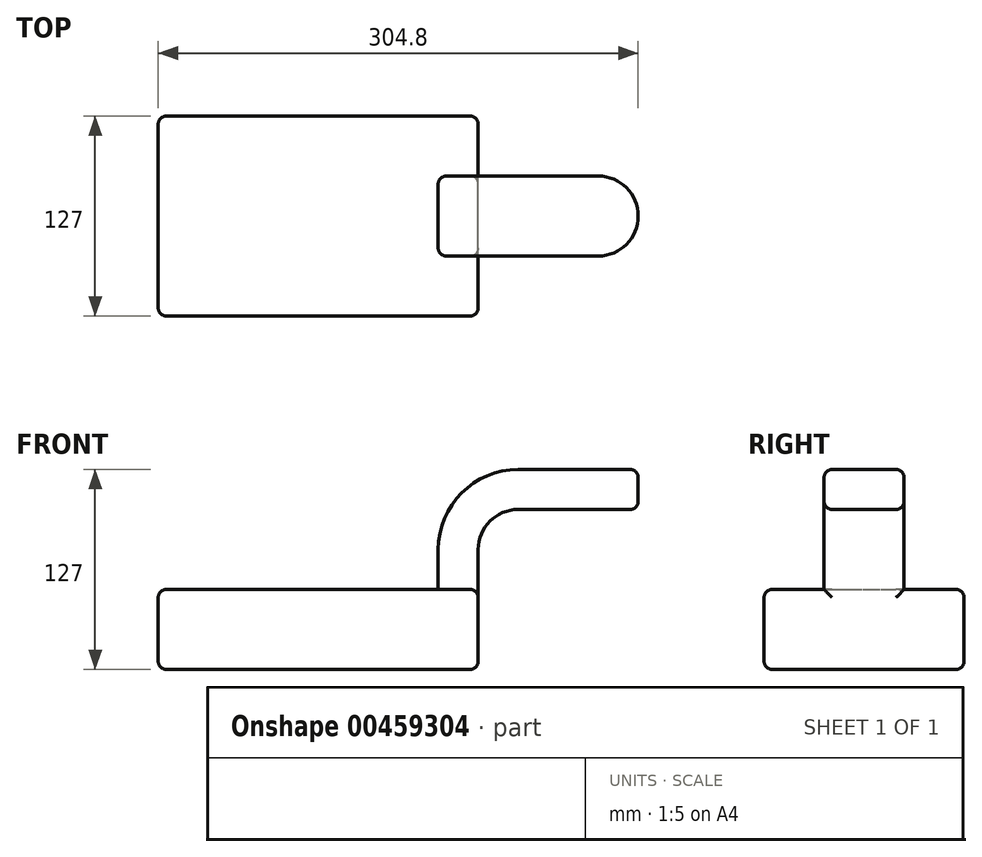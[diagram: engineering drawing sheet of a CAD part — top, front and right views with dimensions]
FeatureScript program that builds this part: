
annotation { "Feature Type Name" : "Feature", "Feature Type Description" : "" }
export const myFeature = defineFeature(function(context is Context, id is Id, definition is map)
    precondition{}
    {
        {
            var Q0;
            Q0=qCreatedBy(makeId("Front.planeOp"),FACE);
            var sketch = newSketch(context, id + "F0", { "sketchPlane" : qUnion([Q0])});
            skLineSegment(sketch, "E0.bottom", {"start": v(-101.6, -25.4) * mm, "end": v(101.6, -25.4) * mm});
            skLineSegment(sketch, "E0.top", {"start": v(-101.6, 25.4) * mm, "end": v(101.6, 25.4) * mm});
            skLineSegment(sketch, "E0.left", {"start": v(-101.6, -25.4) * mm, "end": v(-101.6, 25.4) * mm});
            skLineSegment(sketch, "E0.right", {"start": v(101.6, -25.4) * mm, "end": v(101.6, 25.4) * mm});
            skPoint(sketch, "E0.middle", {"position": v(0, 0) * mm});
            skLineSegment(sketch, "E1.bottom", {"start": v(152.4, 76.2) * mm, "end": v(203.2, 76.2) * mm});
            skLineSegment(sketch, "E1.top", {"start": v(152.4, 127) * mm, "end": v(203.2, 127) * mm});
            skLineSegment(sketch, "E1.left", {"start": v(152.4, 76.2) * mm, "end": v(152.4, 127) * mm});
            skLineSegment(sketch, "E1.right", {"start": v(203.2, 76.2) * mm, "end": v(203.2, 127) * mm});
            skPoint(sketch, "E1.middle", {"position": v(177.8, 101.6) * mm});
            skLineSegment(sketch, "E2", {"start": v(101.6, 25.4) * mm, "end": v(101.6, 50.8) * mm});
            skArc(sketch, "E3", {"start": v(101.6, 50.8) * mm, "mid": v(109.04, 68.76) * mm, "end": v(127, 76.2) * mm});
            skLineSegment(sketch, "E4", {"start": v(127, 76.2) * mm, "end": v(177.8, 76.2) * mm});
            skPoint(sketch, "E4.endSnap0", {"position": v(177.8, 76.2) * mm});
            skLineSegment(sketch, "E5.0", {"start": v(127, 101.6) * mm, "end": v(177.8, 101.6) * mm});
            skArc(sketch, "E5.1", {"start": v(76.2, 50.8) * mm, "mid": v(91.08, 86.72) * mm, "end": v(127, 101.6) * mm});
            skLineSegment(sketch, "E5.2", {"start": v(76.2, 25.4) * mm, "end": v(76.2, 50.8) * mm});
            skLineSegment(sketch, "E6", {"start": v(177.8, 101.6) * mm, "end": v(177.8, 76.2) * mm});
            skFitSpline(sketch, "E7", {"points": [v(127, 101.6) * mm, v(-101.6, 25.4) * mm], "startDerivative": vector(-2.3, 149.1) * mm, "endDerivative": vector(-228.6, -76.2) * mm});
            skLineSegment(sketch, "E8", {"start": v(177.8, 101.6) * mm, "end": v(177.8, 127) * mm});
            skSolve(sketch);
        }
        {
            var Q0;
            Q0=makeQuery(id+"F0.imprint","IMPRINT",FACE,{"disambiguationData":[TD([[makeQuery(id+"F0.imprint","IMPRINT",EDGE,{"derivedFrom":sQuery(id+"F0.wireOp",EDGE,"E0.bottom")}),1.0]])]});
            extrude(context, id + "F1", {"entities" : qUnion([Q0]), "endBound" : BoundingType.SYMMETRIC, "depth" : 127 * mm});
        }
        {
            var Q0;
            {var subQ1=sQuery(id+"F0.wireOp",EDGE,"E2");Q0=makeQuery(id+"F0.imprint","IMPRINT",FACE,{"disambiguationData":[TD([[makeQuery(id+"F0.imprint","IMPRINT",EDGE,{"derivedFrom":subQ1}),1.0]])]});}
            var Q1;
            {var subQ5=sQuery(id+"F0.wireOp",EDGE,"E6");Q1=makeQuery(id+"F0.imprint","IMPRINT",FACE,{"disambiguationData":[TD([[makeQuery(id+"F0.imprint","IMPRINT",EDGE,{"derivedFrom":subQ5}),-1.0]])]});}
            extrude(context, id + "F2", {"entities" : qUnion([Q0, Q1]), "operationType" : NewBodyOperationType.ADD, "endBound" : BoundingType.SYMMETRIC, "depth" : 50.8 * mm});
        }
        {
            var Q0;
            Q0=makeQuery(id+"F0.imprint","IMPRINT",FACE,{"disambiguationData":[TD([[makeQuery(id+"F0.imprint","IMPRINT",EDGE,{"derivedFrom":sQuery(id+"F0.wireOp",EDGE,"E5.1")}),1.0]])]});
            extrude(context, id + "F3", {"entities" : qUnion([Q0]), "operationType" : NewBodyOperationType.ADD, "endBound" : BoundingType.SYMMETRIC, "depth" : 12.7 * mm});
        }
        {
            var Q0;
            Q0=makeQuery(id+"F0.imprint","IMPRINT",FACE,{"disambiguationData":[TD([[makeQuery(id+"F0.imprint","IMPRINT",EDGE,{"derivedFrom":sQuery(id+"F0.wireOp",EDGE,"E1.bottom")}),1.0]])]});
            var Q1;
            Q1=sQuery(id+"F0.wireOp",EDGE,"E8");
            revolve(context, id + "F4", {"operationType" : NewBodyOperationType.ADD, "entities" : qUnion([Q0]), "axis" : qUnion([Q1]), "revolveType" : RevolveType.FULL});
        }
        {
            var Q0;
            Q0=makeQuery(id+"F1.opExtrude","CAP_EDGE",EDGE,{"disambiguationData":[OSD([sQuery(id+"F0.wireOp",EDGE,"E0.right")])],"isStart":false});
            var Q1;
            Q1=makeQuery(id+"F1.opExtrude","CAP_EDGE",EDGE,{"disambiguationData":[OSD([sQuery(id+"F0.wireOp",EDGE,"E0.left")])],"isStart":false});
            var Q2;
            Q2=makeQuery(id+"F1.opExtrude","CAP_EDGE",EDGE,{"disambiguationData":[OSD([sQuery(id+"F0.wireOp",EDGE,"E0.right")])],"isStart":true});
            var Q3;
            Q3=makeQuery(id+"F1.opExtrude","CAP_EDGE",EDGE,{"disambiguationData":[OSD([sQuery(id+"F0.wireOp",EDGE,"E0.left")])],"isStart":true});
            var Q4;
            Q4=makeQuery(id+"F1.opExtrude","CAP_EDGE",EDGE,{"disambiguationData":[OSD([sQuery(id+"F0.wireOp",EDGE,"E0.top")])],"isStart":true});
            var Q5;
            Q5=makeQuery(id+"F1.opExtrude","CAP_EDGE",EDGE,{"disambiguationData":[OSD([sQuery(id+"F0.wireOp",EDGE,"E0.bottom")])],"isStart":true});
            var Q6;
            Q6=makeQuery(id+"F1.opExtrude","SWEPT_EDGE",EDGE,{"disambiguationData":[OSD([sQuery(id+"F0.wireOp",EDGE,"E0.bottom"),sQuery(id+"F0.wireOp",EDGE,"E0.right")])]});
            var Q7;
            {var subQ0=sQuery(id+"F0.wireOp",EDGE,"E2");var subQ1=sQuery(id+"F0.wireOp",EDGE,"E0.top");var subQ2=sQuery(id+"F0.wireOp",EDGE,"E0.right");Q7=makeQuery(id+"F2.boolean.opBoolean","SPLIT",EDGE,{"disambiguationData":[TD([makeQuery(id+"F1.opExtrude","CAP_FACE",FACE,{"disambiguationData":[OSD([sQuery(id+"F0.wireOp",EDGE,"E0.bottom"),subQ1,sQuery(id+"F0.wireOp",EDGE,"E0.left"),subQ2])],"isStart":true})])],"derivedFrom":makeQuery(id+"F1.opExtrude","SWEPT_EDGE",EDGE,{"disambiguationData":[OSD([subQ1,subQ2,subQ0])]})});}
            var Q8;
            Q8=makeQuery(id+"F2.opExtrude","CAP_EDGE",EDGE,{"disambiguationData":[OSD([sQuery(id+"F0.wireOp",EDGE,"E2")])],"isStart":true});
            var Q9;
            Q9=makeQuery(id+"F2.opExtrude","CAP_EDGE",EDGE,{"disambiguationData":[OSD([sQuery(id+"F0.wireOp",EDGE,"E3")])],"isStart":true});
            var Q10;
            {var subQ0=sQuery(id+"F0.wireOp",EDGE,"E0.right");var subQ1=sQuery(id+"F0.wireOp",EDGE,"E2");var subQ2=sQuery(id+"F0.wireOp",EDGE,"E0.top");Q10=makeQuery(id+"F2.boolean.opBoolean","SPLIT",EDGE,{"disambiguationData":[TD([makeQuery(id+"F1.opExtrude","CAP_FACE",FACE,{"disambiguationData":[OSD([sQuery(id+"F0.wireOp",EDGE,"E0.bottom"),subQ2,sQuery(id+"F0.wireOp",EDGE,"E0.left"),subQ0])],"isStart":false})])],"derivedFrom":makeQuery(id+"F1.opExtrude","SWEPT_EDGE",EDGE,{"disambiguationData":[OSD([subQ2,subQ0,subQ1])]})});}
            var Q11;
            Q11=makeQuery(id+"F1.opExtrude","CAP_FACE",FACE,{"disambiguationData":[OSD([sQuery(id+"F0.wireOp",EDGE,"E0.bottom"),sQuery(id+"F0.wireOp",EDGE,"E0.top"),sQuery(id+"F0.wireOp",EDGE,"E0.left"),sQuery(id+"F0.wireOp",EDGE,"E0.right")])],"isStart":false});
            var Q12;
            {var subQ0=sQuery(id+"F0.wireOp",EDGE,"E7");var subQ1=sQuery(id+"F0.wireOp",EDGE,"E0.top");var subQ2=sQuery(id+"F0.wireOp",EDGE,"E0.left");Q12=makeQuery(id+"F3.boolean.opBoolean","SPLIT",EDGE,{"disambiguationData":[TD([makeQuery(id+"F1.opExtrude","CAP_FACE",FACE,{"disambiguationData":[OSD([sQuery(id+"F0.wireOp",EDGE,"E0.bottom"),subQ1,subQ2,sQuery(id+"F0.wireOp",EDGE,"E0.right")])],"isStart":false})])],"derivedFrom":makeQuery(id+"F1.opExtrude","SWEPT_EDGE",EDGE,{"disambiguationData":[OSD([subQ1,subQ2,subQ0])]})});}
            var Q13;
            Q13=makeQuery(id+"F1.opExtrude","SWEPT_EDGE",EDGE,{"disambiguationData":[OSD([sQuery(id+"F0.wireOp",EDGE,"E0.bottom"),sQuery(id+"F0.wireOp",EDGE,"E0.left")])]});
            var Q14;
            Q14=makeQuery(id+"F3.opExtrude","CAP_EDGE",EDGE,{"disambiguationData":[OSD([sQuery(id+"F0.wireOp",EDGE,"E7")])],"isStart":true});
            fillet(context, id + "F5", {"entities" : qUnion([Q0, Q1, Q2, Q3, Q4, Q5, Q6, Q7, Q8, Q9, Q10, Q11, Q12, Q13, Q14]), "radius" : 5.08 * mm, "tangentPropagation" : true, "allowEdgeOverflow" : false});
        }
        {
            var Q0;
            {var subQ0=sQuery(id+"F0.wireOp",EDGE,"E7");var subQ1=sQuery(id+"F0.wireOp",EDGE,"E0.left");var subQ2=sQuery(id+"F0.wireOp",EDGE,"E0.top");Q0=makeQuery(id+"F3.boolean.opBoolean","MERGE",EDGE,{"derivedFrom":[makeQuery(id+"F1.opExtrude","SWEPT_EDGE",EDGE,{"disambiguationData":[OSD([subQ2,subQ1,subQ0])]}),makeQuery(id+"F3.opExtrude","SWEPT_EDGE",EDGE,{"disambiguationData":[OSD([subQ2,subQ1,subQ0])]})]});}
            var Q1;
            Q1=makeQuery(id+"F3.opExtrude","CAP_EDGE",EDGE,{"disambiguationData":[OSD([sQuery(id+"F0.wireOp",EDGE,"E7")])],"isStart":false});
            var Q2;
            Q2=makeQuery(id+"F2.opExtrude","CAP_EDGE",EDGE,{"disambiguationData":[OSD([sQuery(id+"F0.wireOp",EDGE,"E5.2")])],"isStart":false});
            var Q3;
            Q3=makeQuery(id+"F2.opExtrude","CAP_EDGE",EDGE,{"disambiguationData":[OSD([sQuery(id+"F0.wireOp",EDGE,"E5.1")])],"isStart":true});
            var Q4;
            Q4=makeQuery(id+"F4.opRevolve","SWEPT_FACE",FACE,{"disambiguationData":[OSD([sQuery(id+"F0.wireOp",EDGE,"E1.top")])]});
            fillet(context, id + "F6", {"entities" : qUnion([Q0, Q1, Q2, Q3, Q4]), "radius" : 5.08 * mm, "tangentPropagation" : true, "allowEdgeOverflow" : false});
        }
    });
